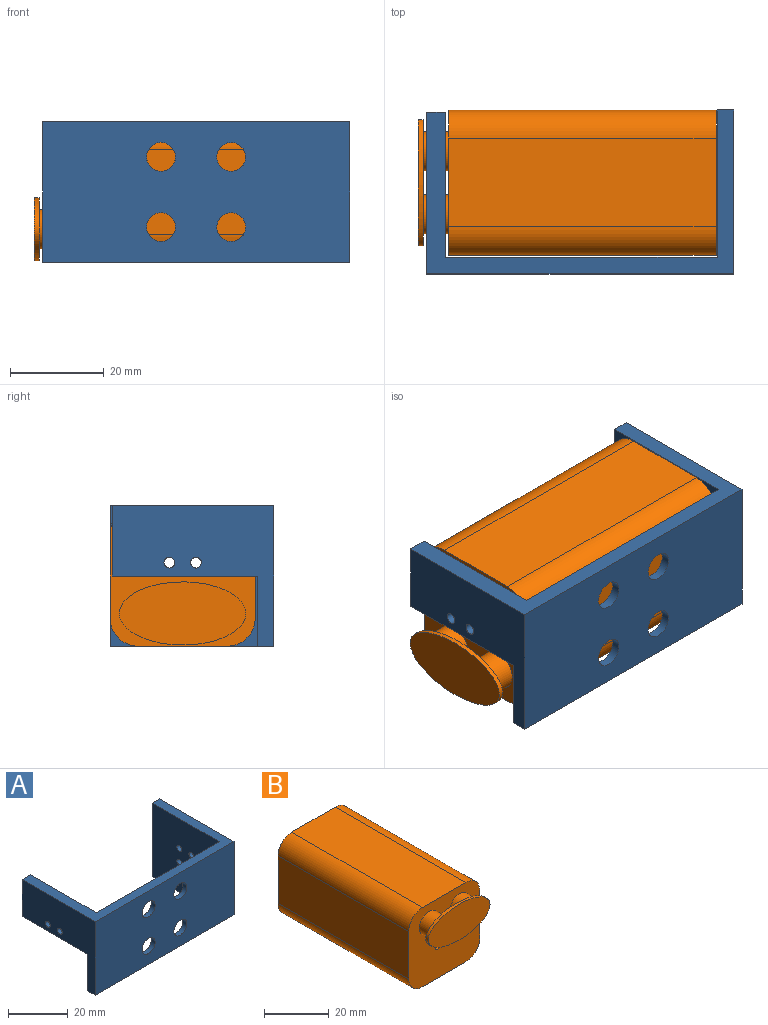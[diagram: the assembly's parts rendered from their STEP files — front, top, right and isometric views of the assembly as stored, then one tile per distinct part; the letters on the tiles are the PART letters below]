
ASSEMBLY  parts=2 mates=1
PART A: 29 faces, bbox 65.6x35x30 mm
  f0: cylinder r=3.09mm len=6.18mm, axis (0,1,0), area 36.9mm2, adj f8,f27
  f1: cylinder r=3.09mm len=6.18mm, axis (0,1,0), area 36.9mm2, adj f8,f25
  f2: cylinder r=3.09mm len=6.18mm, axis (0,1,0), area 36.9mm2, adj f8,f23
  f3: cylinder r=3.09mm len=6.18mm, axis (0,1,0), area 36.9mm2, adj f8,f21
  f4: plane 35x30mm, normal (1,0,0), area 1033.4mm2, adj f5,f7,f8,f10,f17,f18,f19,f20
  f5: plane 65.6x35mm, normal (0,0,1), area 463.9mm2, adj f4,f6,f8,f9,f10,f11,f12,f13
  f6: plane 34.5x30mm, normal (-1,0,0), area 561.7mm2, adj f5,f7,f8,f9,f12,f14,f15,f16
  f7: plane 65.6x35mm, normal (0,0,-1), area 339.9mm2, adj f4,f6,f8,f9,f10,f11
  f8: plane 65.6x30mm, normal (0,-1,0), area 1848.2mm2, adj f0,f1,f2,f3,f4,f5,f6,f7
  f9: plane 62.1x30mm, normal (0,1,0), area 1362.4mm2, adj f5,f6,f7,f11,f13,f14,f22,f24
  f10: plane 30x3.5mm, normal (0,1,0), area 105mm2, adj f4,f5,f7,f11
  f11: plane 31.5x30mm, normal (-1,0,0), area 928.4mm2, adj f5,f7,f9,f10,f17,f18,f19,f20
  f12: plane 15x4mm, normal (0,1,0), area 60mm2, adj f5,f6,f13,f14
  f13: plane 31x15mm, normal (1,0,0), area 456.7mm2, adj f5,f9,f12,f14,f15,f16
  f14: plane 31x4mm, normal (0,0,-1), area 124mm2, adj f6,f9,f12,f13
  f15: cylinder r=1.15mm len=4mm, axis (1,0,0), area 28.9mm2, adj f6,f13
  f16: cylinder r=1.15mm len=4mm, axis (1,0,0), area 28.9mm2, adj f6,f13
  f17: cylinder r=1.15mm len=3.5mm, axis (1,0,0), area 25.3mm2, adj f4,f11
  f18: cylinder r=1.15mm len=3.5mm, axis (1,0,0), area 25.3mm2, adj f4,f11
  f19: cylinder r=1.15mm len=3.5mm, axis (1,0,0), area 25.3mm2, adj f4,f11
  f20: cylinder r=1.15mm len=3.5mm, axis (1,0,0), area 25.3mm2, adj f4,f11
  f21: plane 11.84x11.84mm, normal (0,1,0), area 80.2mm2, adj f3,f22
  f22: cylinder r=5.92mm len=11.84mm, axis (0,1,0), area 59.5mm2, adj f9,f21
  f23: plane 11.84x11.84mm, normal (0,1,0), area 80.2mm2, adj f2,f24
  f24: cylinder r=5.92mm len=11.84mm, axis (0,1,0), area 59.5mm2, adj f9,f23
  f25: plane 11.84x11.84mm, normal (0,1,0), area 80.2mm2, adj f1,f26
  f26: cylinder r=5.92mm len=11.84mm, axis (0,1,0), area 59.5mm2, adj f9,f25
  f27: plane 11.84x11.84mm, normal (0,1,0), area 80.2mm2, adj f0,f28
  f28: cylinder r=5.92mm len=11.84mm, axis (0,1,0), area 59.5mm2, adj f9,f27
PART B: 19 faces, bbox 31x63.6x30 mm
  f0: plane 57.1x18mm, normal (1,0,0), area 1027.8mm2, adj f4,f5,f15,f18
  f1: plane 57.1x19mm, normal (0,0,1), area 1084.9mm2, adj f4,f5,f15,f16
  f2: plane 57.1x18mm, normal (-1,0,0), area 1027.8mm2, adj f4,f5,f16,f17
  f3: plane 57.1x19mm, normal (0,0,-1), area 1084.9mm2, adj f4,f5,f17,f18
  f4: plane 31x30mm, normal (0,-1,0), area 773mm2, adj f0,f1,f2,f3,f6,f7,f8,f9
  f5: plane 31x30mm, normal (0,1,0), area 882.5mm2, adj f0,f1,f2,f3,f6,f7,f8,f9
  f6: cylinder r=1.15mm len=57.1mm, axis (0,1,0), area 412.6mm2, adj f4,f5
  f7: cylinder r=1.15mm len=57.1mm, axis (0,1,0), area 412.6mm2, adj f4,f5
  f8: cylinder r=1.15mm len=57.1mm, axis (0,1,0), area 412.6mm2, adj f4,f5
  f9: cylinder r=1.15mm len=57.1mm, axis (0,1,0), area 412.6mm2, adj f4,f5
  f10: cylinder r=4.17mm len=8.35mm, axis (0,1,0), area 144.3mm2, adj f4,f14
  f11: cylinder r=4.17mm len=8.35mm, axis (0,1,0), area 144.3mm2, adj f4,f14
  f12: extruded ~27x13.5mm, area 65.4mm2, adj f13,f14
  f13: plane 27x13.5mm, normal (0,-1,0), area 286.3mm2, adj f12
  f14: plane 27x13.5mm, normal (0,1,0), area 176.8mm2, adj f10,f11,f12
  f15: cylinder r=6mm len=57.1mm, axis (0,1,0), area 538.2mm2, adj f0,f1,f4,f5
  f16: cylinder r=6mm len=57.1mm, axis (0,-1,0), area 538.2mm2, adj f1,f2,f4,f5
  f17: cylinder r=6mm len=57.1mm, axis (0,1,0), area 538.2mm2, adj f2,f3,f4,f5
  f18: cylinder r=6mm len=57.1mm, axis (0,-1,0), area 538.2mm2, adj f0,f3,f4,f5
PLACE A t=(-4.79,5.39,3.63)mm
PLACE B rot(axis=(-0.71,-0.71,0),180deg) t=(-4.29,23.14,3.63)mm
MATE revolute B.f7 <-> A.f15  axis (1,0,0) through (24.26,20.29,6.48)mm
